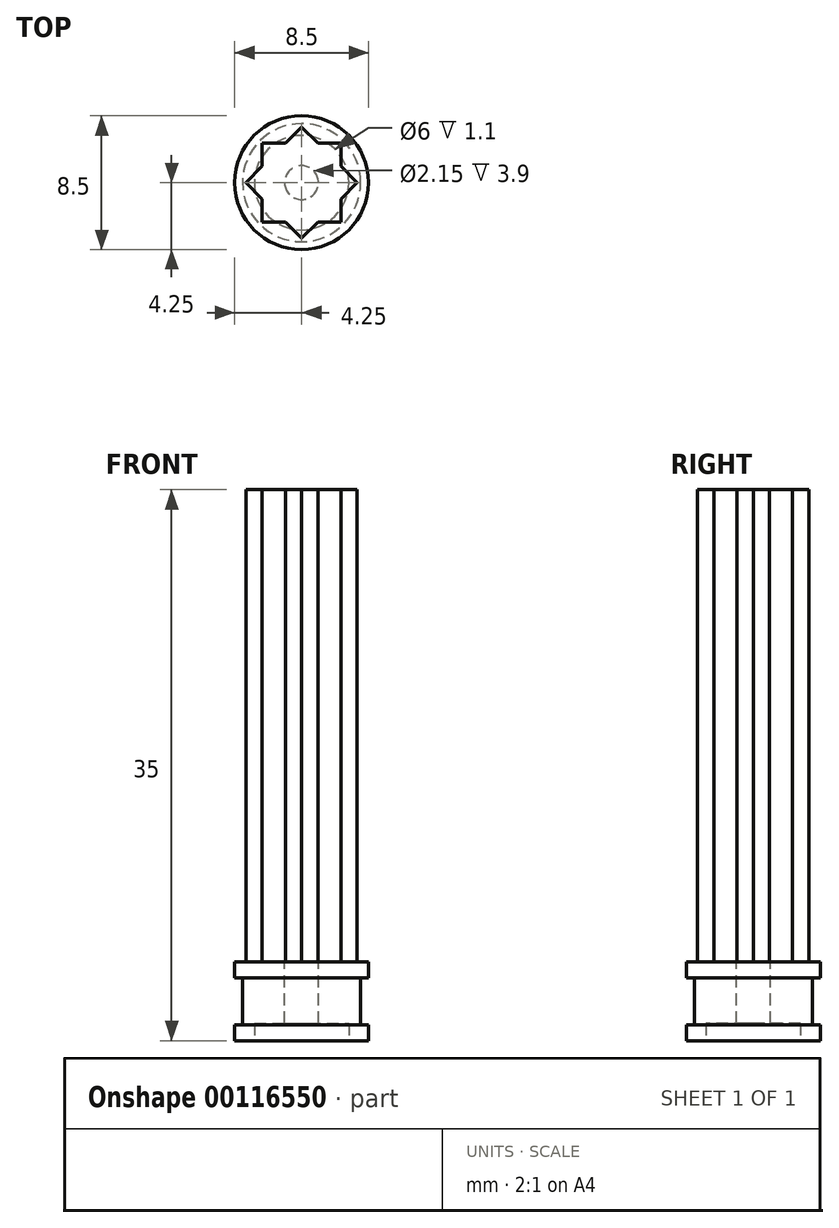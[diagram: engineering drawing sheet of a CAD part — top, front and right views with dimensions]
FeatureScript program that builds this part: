
annotation { "Feature Type Name" : "Feature", "Feature Type Description" : "" }
export const myFeature = defineFeature(function(context is Context, id is Id, definition is map)
    precondition{}
    {
        {
            var Q0;
            Q0=qCreatedBy(makeId("Top.planeOp"),FACE);
            var sketch = newSketch(context, id + "F0", { "sketchPlane" : qUnion([Q0])});
            skLineSegment(sketch, "E0.bottom", {"start": v(-2.5, -2.5) * mm, "end": v(2.5, -2.5) * mm});
            skLineSegment(sketch, "E0.top", {"start": v(-2.5, 2.5) * mm, "end": v(2.5, 2.5) * mm});
            skLineSegment(sketch, "E0.left", {"start": v(-2.5, -2.5) * mm, "end": v(-2.5, 2.5) * mm});
            skLineSegment(sketch, "E0.right", {"start": v(2.5, -2.5) * mm, "end": v(2.5, 2.5) * mm});
            skPoint(sketch, "E0.middle", {"position": v(0, 0) * mm});
            skLineSegment(sketch, "E1", {"start": v(0, 3.54) * mm, "end": v(3.54, 0) * mm});
            skLineSegment(sketch, "E2", {"start": v(3.54, 0) * mm, "end": v(0, -3.54) * mm});
            skLineSegment(sketch, "E3", {"start": v(0, -3.54) * mm, "end": v(-3.54, 0) * mm});
            skLineSegment(sketch, "E4", {"start": v(-3.54, 0) * mm, "end": v(0, 3.54) * mm});
            skSolve(sketch);
        }
        {
            var Q0;
            Q0=qSketchRegion(id+"F0",true);
            extrude(context, id + "F1", {"entities" : qUnion([Q0]), "depth" : 30 * mm});
        }
        {
            var Q0;
            Q0=makeQuery(id+"F1.opExtrude","CAP_FACE",FACE,{"disambiguationData":[OSD([sQuery(id+"F0.wireOp",EDGE,"E0.bottom"),sQuery(id+"F0.wireOp",EDGE,"E0.top"),sQuery(id+"F0.wireOp",EDGE,"E0.left"),sQuery(id+"F0.wireOp",EDGE,"E0.right"),sQuery(id+"F0.wireOp",EDGE,"E1"),sQuery(id+"F0.wireOp",EDGE,"E2"),sQuery(id+"F0.wireOp",EDGE,"E3"),sQuery(id+"F0.wireOp",EDGE,"E4")])],"isStart":true});
            var sketch = newSketch(context, id + "F2", { "sketchPlane" : qUnion([Q0])});
            skCircle(sketch, "E5", {"center": v(0, 0) * mm, "radius": 4.25 * mm});
            skSolve(sketch);
        }
        {
            var Q0;
            Q0=qSketchRegion(id+"F2",true);
            extrude(context, id + "F3", {"entities" : qUnion([Q0]), "operationType" : NewBodyOperationType.ADD, "depth" : 5 * mm});
        }
        {
            var Q0;
            Q0=makeQuery(id+"F3.opExtrude","CAP_FACE",FACE,{"disambiguationData":[OSD([sQuery(id+"F2.wireOp",EDGE,"E5")])],"isStart":false});
            cPlane(context, id + "F4", {"entities" : qUnion([Q0]), "cplaneType" : CPlaneType.OFFSET, "offset" : 1 * mm, "oppositeDirection" : true, "width" : 150 * mm, "height" : 150 * mm});
        }
        {
            var Q0;
            Q0=qCreatedBy(id+"F4.planeOp",FACE);
            var sketch = newSketch(context, id + "F5", { "sketchPlane" : qUnion([Q0])});
            skCircle(sketch, "E6", {"center": v(0, 0) * mm, "radius": 4.25 * mm});
            skCircle(sketch, "E7", {"center": v(0, 0) * mm, "radius": 3.75 * mm});
            skSolve(sketch);
        }
        {
            var Q0;
            Q0=qSketchRegion(id+"F5",true);
            extrude(context, id + "F6", {"entities" : qUnion([Q0]), "operationType" : NewBodyOperationType.REMOVE, "oppositeDirection" : true, "depth" : 3 * mm});
        }
        {
            var Q0;
            Q0=qCreatedBy(makeId("Top.planeOp"),FACE);
            var sketch = newSketch(context, id + "F7", { "sketchPlane" : qUnion([Q0])});
            skCircle(sketch, "E8", {"center": v(0, 0) * mm, "radius": 1.07 * mm});
            skSolve(sketch);
        }
        {
            var Q0;
            Q0=qSketchRegion(id+"F7",true);
            extrude(context, id + "F8", {"entities" : qUnion([Q0]), "operationType" : NewBodyOperationType.REMOVE, "oppositeDirection" : true, "depth" : 5 * mm});
        }
        {
            var Q0;
            Q0=makeQuery(id+"F3.opExtrude","CAP_FACE",FACE,{"disambiguationData":[OSD([sQuery(id+"F2.wireOp",EDGE,"E5")])],"isStart":false});
            var sketch = newSketch(context, id + "F9", { "sketchPlane" : qUnion([Q0])});
            skCircle(sketch, "E9", {"center": v(0, 0) * mm, "radius": 3 * mm});
            skSolve(sketch);
        }
        {
            var Q0;
            Q0 = qSketchRegion(id + "F9", true);
            extrude(context, id + "F10", {"entities" : qUnion([Q0]), "operationType" : NewBodyOperationType.REMOVE, "oppositeDirection" : true, "depth" : 1.1 * mm});
        }
    });
